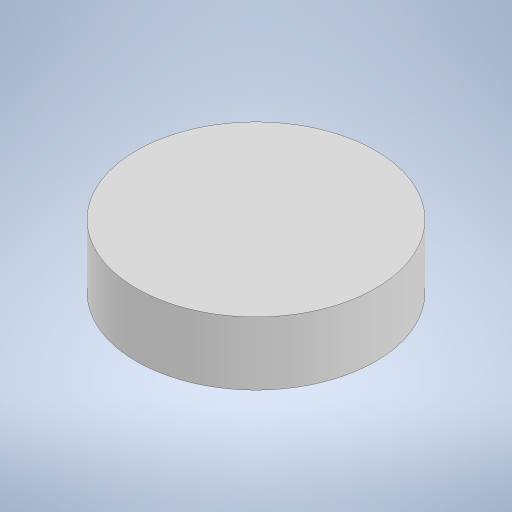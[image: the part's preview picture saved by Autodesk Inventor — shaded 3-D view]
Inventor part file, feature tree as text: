
AUTODESK INVENTOR PART (.ipt)
format: ipt  version: 2023 (Build 270158000, 158)  size: 729,600 bytes
history: native  units: in
note: dims shown in document units (in); Inventor stores cm internally (conversion verified against a paired STEP export)
features: extrude x4, sketch x4, helix x1, chamfer x1, projected_geometry x1
ambient origin geometry x8: Origin, YZ Plane, XZ Plane, XY Plane, X Axis, Y Axis, Z Axis, Center Point
bodies: Solid1 (feature_tree)
feature tree (11):
  extrude  "Extrusion1"  Depth=0.063in
  sketch  "Sketch2"  dims[d2=0.126in d3=0.0in d4=2.7677in]
  extrude  "Extrusion2"  Depth=2.7677in
  extrude  "Extrusion3"  Depth=0.7087in
  helix  "Coil1"  [1 undecoded]
  chamfer  "Chamfer1"  Distance=0.1181in
  extrude  "Extrusion4"  Depth=0.3937in
  sketch  "Sketch1"  dims[d0=2.2756in d1=0.063in]
  sketch  "Sketch3"  dims[d5=3.1181in d6=0.1122in d7=0.7087in d8=0.0in d9=0.1181in d10=0.0in]
  projected_geometry  "Projected Loop1"
  sketch  "Sketch5"  dims[d12=0.0787in d13=0.1102in d14=1.4016in d15=0.1457in d16=0.6299in d17=0.9449in d18=0.0in d19=90.0deg d20=90.0deg d21=0.0in d22=0.0in d24=0.0984in d25=0.0787in d26=30.0deg d27=0.3937in d28=0.0in d29=0.0in d30=0.0in]
note: 1 required parameter value undecoded (feature->parameter linkage not recoverable at this tier; creation-order binding heuristic only, values carry confidence <= 0.55)
